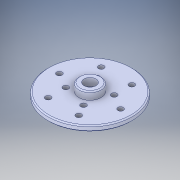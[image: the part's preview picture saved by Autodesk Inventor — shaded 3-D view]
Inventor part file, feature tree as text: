
AUTODESK INVENTOR PART (.ipt)
format: ipt  version: 2018 (Build 220112000, 112)  size: 153,600 bytes
history: native  units: in
note: dims shown in document units (in); Inventor stores cm internally (conversion verified against a paired STEP export)
features: chamfer x1
ambient origin geometry x8: Origin, YZ Plane, XZ Plane, XY Plane, X Axis, Y Axis, Z Axis, Center Point
bodies: Solid1 (feature_tree)
feature tree (1):
  chamfer  "Chamfer1"  [1 undecoded]
note: 1 required parameter value undecoded (feature->parameter linkage not recoverable at this tier; creation-order binding heuristic only, values carry confidence <= 0.55)
